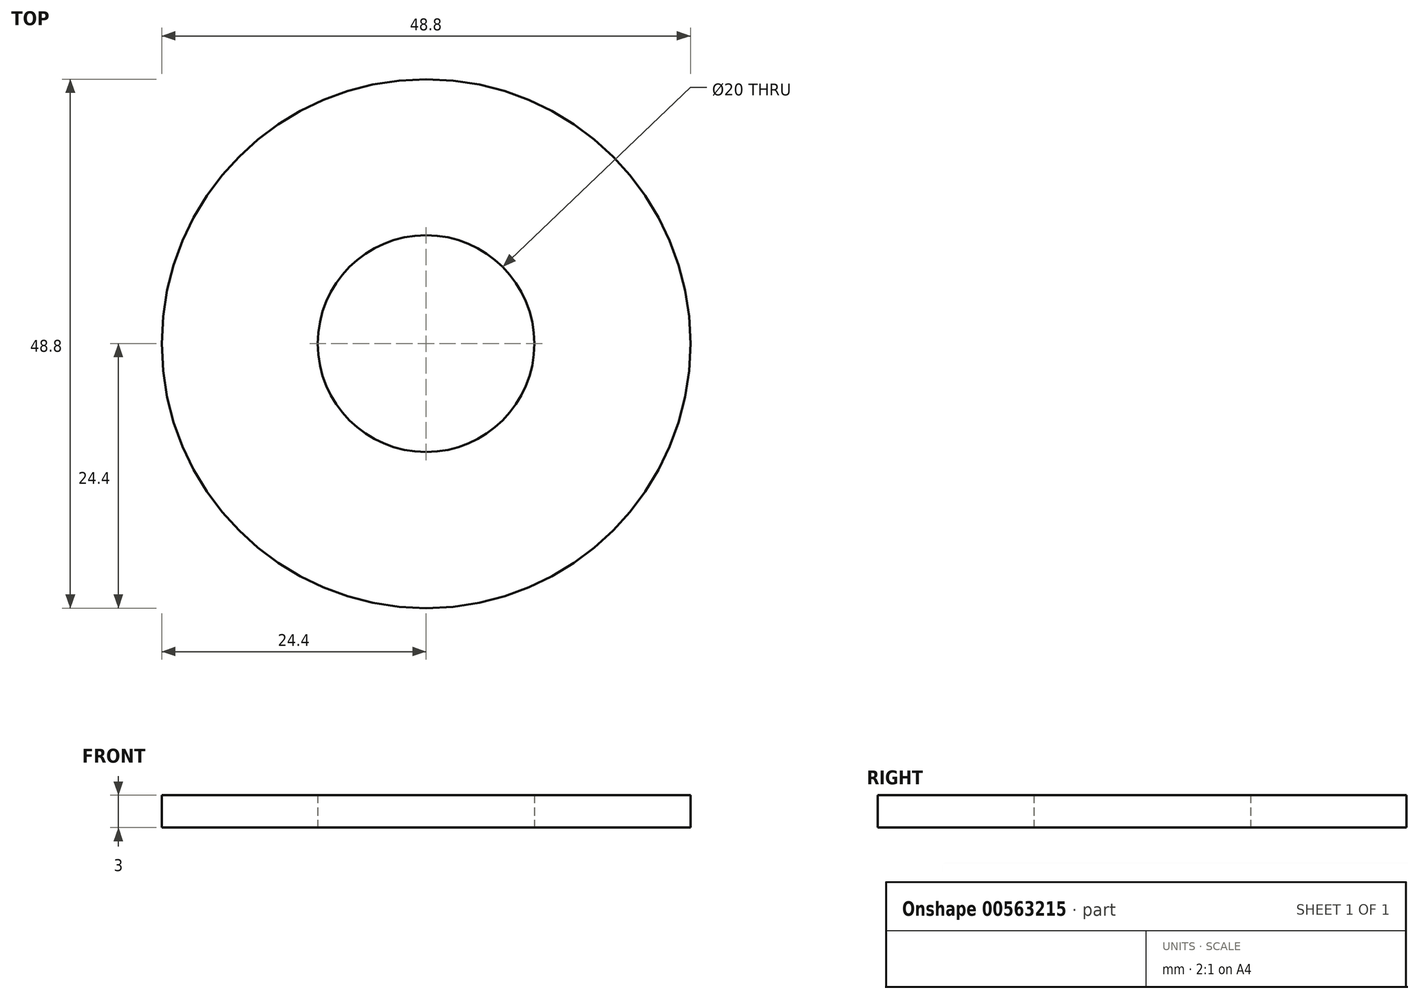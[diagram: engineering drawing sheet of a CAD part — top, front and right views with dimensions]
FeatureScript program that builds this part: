
annotation { "Feature Type Name" : "Feature", "Feature Type Description" : "" }
export const myFeature = defineFeature(function(context is Context, id is Id, definition is map)
    precondition{}
    {
        {
            var Q0;
            Q0=qCreatedBy(makeId("Top.planeOp"),FACE);
            var sketch = newSketch(context, id + "F0", { "sketchPlane" : qUnion([Q0])});
            skCircle(sketch, "E0", {"center": v(0, 0) * mm, "radius": 10 * mm});
            skCircle(sketch, "E1", {"center": v(0, 0) * mm, "radius": 24.4 * mm});
            skSolve(sketch);
        }
        {
            var Q0;
            Q0=qSketchRegion(id+"F0",true);
            extrude(context, id + "F1", {"entities" : qUnion([Q0]), "endBound" : BoundingType.SYMMETRIC, "depth" : 3 * mm, "offsetDistance" : 25 * mm});
        }
    });
